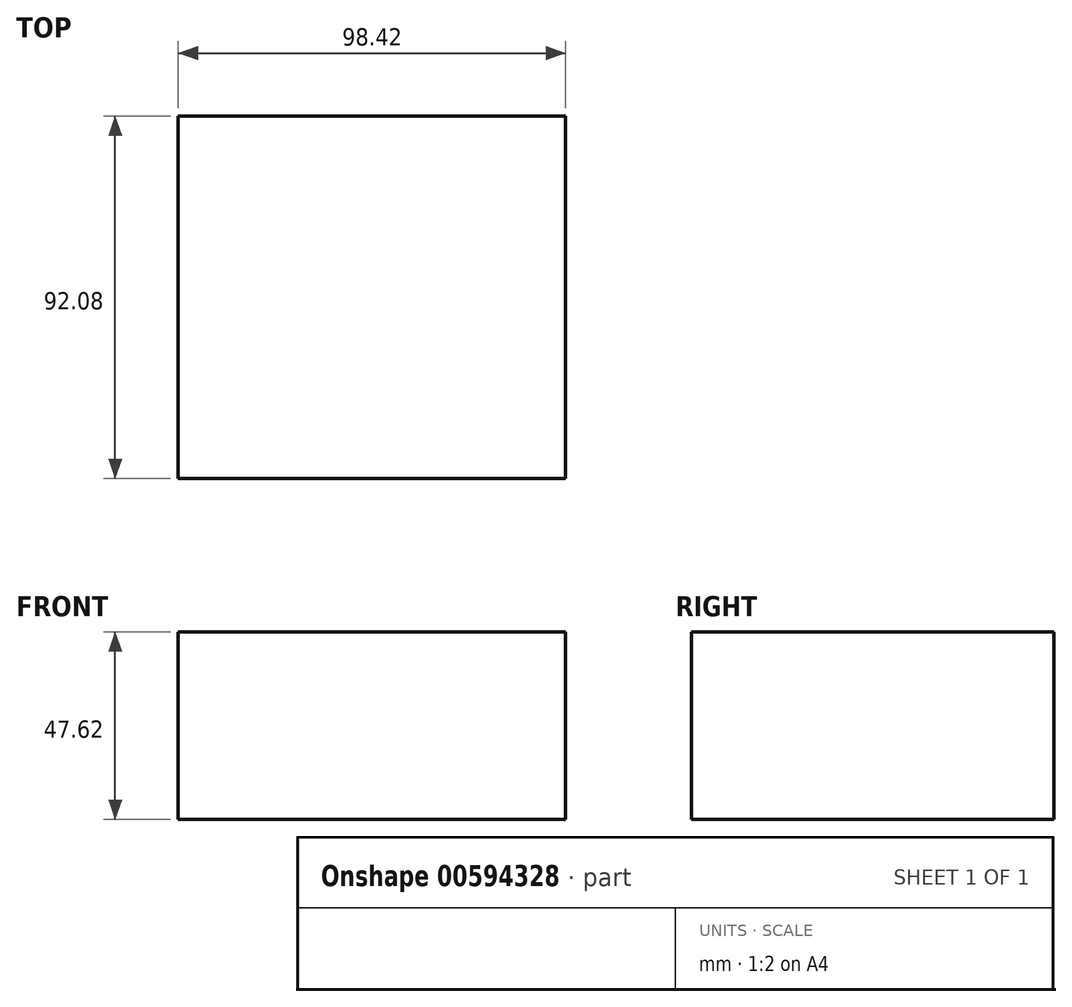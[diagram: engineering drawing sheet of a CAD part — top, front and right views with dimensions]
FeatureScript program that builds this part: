
annotation { "Feature Type Name" : "Feature", "Feature Type Description" : "" }
export const myFeature = defineFeature(function(context is Context, id is Id, definition is map)
    precondition{}
    {
        {
            var Q0;
            Q0=qCreatedBy(makeId("Front.planeOp"),FACE);
            var sketch = newSketch(context, id + "F0", { "sketchPlane" : qUnion([Q0])});
            skLineSegment(sketch, "E0", {"start": v(0, 0) * mm, "end": v(98.43, 0) * mm});
            skLineSegment(sketch, "E1", {"start": v(98.43, 0) * mm, "end": v(98.43, 47.63) * mm});
            skLineSegment(sketch, "E2", {"start": v(98.43, 47.63) * mm, "end": v(0, 47.63) * mm});
            skLineSegment(sketch, "E3", {"start": v(0, 47.63) * mm, "end": v(0, 0) * mm});
            skLineSegment(sketch, "E4", {"start": v(0, 0) * mm, "end": v(41.54, 0) * mm});
            skSolve(sketch);
        }
        {
            var Q0;
            Q0 = qSketchRegion(id + "F0", true);
            extrude(context, id + "F1", {"entities" : qUnion([Q0]), "depth" : 25.4 * mm, "offsetDistance" : 25.4 * mm});
        }
        {
            var Q0;
            Q0=makeQuery(id+"F1.opExtrude","CAP_FACE",FACE,{"disambiguationData":[OSD([sQuery(id+"F0.wireOp",EDGE,"E0"),sQuery(id+"F0.wireOp",EDGE,"E1"),sQuery(id+"F0.wireOp",EDGE,"E2"),sQuery(id+"F0.wireOp",EDGE,"E3")])],"isStart":false});
            extrude(context, id + "F2", {"entities" : qUnion([Q0]), "operationType" : NewBodyOperationType.ADD, "depth" : 66.67 * mm, "offsetDistance" : 25.4 * mm});
        }
    });
